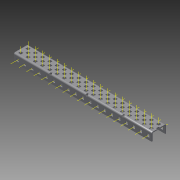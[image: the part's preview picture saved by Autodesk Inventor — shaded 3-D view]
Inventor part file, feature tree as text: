
AUTODESK INVENTOR PART (.ipt)
format: ipt  version: 2015 (Build 190159000, 159)  size: 2,113,024 bytes
history: native  units: in
note: dims shown in document units (in); Inventor stores cm internally (conversion verified against a paired STEP export)
features: other x101, pattern_linear x3, sheet_metal_op x1, extrude x1, imported_body x1, sketch x1
ambient origin geometry x8: Origin, YZ Plane, XZ Plane, XY Plane, X Axis, Y Axis, Z Axis, Center Point
bodies: Body1 (feature_tree)
feature tree (108):
  sheet_metal_op  "Fold1"
  other  "C-Channel"
  extrude  "length cut"  Depth=0.5in
  other  "top axis"
  other  "inner axis"
  other  "front axis"
  other  "back axis"
  pattern_linear  "top axes"  Spacing1=0.5in  [1 undecoded]
  pattern_linear  "inner axes"  Spacing1=0.5in  [1 undecoded]
  pattern_linear  "horiz axes"  Spacing1=-9.5in  [1 undecoded]
  other  "right plane"
  imported_body  "Base1"
  sketch  "Sketch1"  dims[d1=0.0in d4=0.5in d5=0.7874in d7=0.5in d10=0.5in d13=0.5in d14=-9.5in d15=0.0in d16=0.0in d17=0.0in d18=0.0in d19=0.0in]
  other  "Work Point1"
  other  "Work Point2"
  other  "Work Point3"
  other  "Work Point4"
  other  "Work Axis5"
  other  "Work Axis6"
  other  "Work Axis7"
  other  "Work Axis8"
  other  "Work Axis11"
  other  "Work Axis12"
  other  "Work Axis13"
  other  "Work Axis14"
  other  "Work Axis15"
  other  "Work Axis18"
  other  "Work Axis19"
  other  "Work Axis20"
  other  "Work Axis23"
  other  "Work Axis24"
  other  "Work Axis25"
  other  "Work Axis26"
  other  "Work Axis30"
  other  "Work Axis31"
  other  "Work Axis32"
  other  "Work Axis33"
  other  "left plane"
  other  "Work Axis37"
  other  "Work Axis38"
  other  "Work Axis39"
  other  "Work Axis40"
  other  "Work Axis41"
  other  "Work Axis42"
  other  "Work Axis43"
  other  "Work Axis44"
  other  "Work Axis45"
  other  "Work Axis46"
  other  "Work Axis47"
  other  "Work Axis48"
  other  "Work Axis49"
  other  "Work Axis50"
  other  "Work Axis57"
  other  "Work Axis58"
  other  "Work Axis59"
  other  "Work Axis60"
  other  "Work Axis61"
  other  "Work Axis62"
  other  "Work Axis63"
  other  "Work Axis64"
  other  "Work Axis65"
  other  "Work Axis66"
  other  "Work Axis67"
  other  "Work Axis68"
  other  "Work Axis69"
  other  "Work Axis70"
  other  "Work Axis77"
  other  "Work Axis78"
  other  "Work Axis79"
  other  "Work Axis80"
  other  "Work Axis81"
  other  "Work Axis82"
  other  "Work Axis83"
  other  "Work Axis84"
  other  "Work Axis85"
  other  "Work Axis86"
  other  "Work Axis87"
  other  "Work Axis88"
  other  "Work Axis89"
  other  "Work Axis90"
  other  "Work Axis97"
  other  "Work Axis98"
  other  "Work Axis99"
  other  "Work Axis100"
  other  "Work Axis101"
  other  "Work Axis102"
  other  "Work Axis103"
  other  "Work Axis104"
  other  "Work Axis105"
  other  "Work Axis106"
  other  "Work Axis107"
  other  "Work Axis108"
  other  "Work Axis109"
  other  "Work Axis110"
  other  "Work Axis117"
  other  "Work Axis118"
  other  "Work Axis119"
  other  "Work Axis120"
  other  "Work Axis121"
  other  "Work Axis122"
  other  "Work Axis123"
  other  "Work Axis124"
  other  "Work Axis125"
  other  "Work Axis126"
  other  "Work Axis127"
  other  "Work Axis128"
  other  "Work Axis129"
  other  "Work Axis130"
note: 3 required parameter values undecoded (feature->parameter linkage not recoverable at this tier; creation-order binding heuristic only, values carry confidence <= 0.55)
